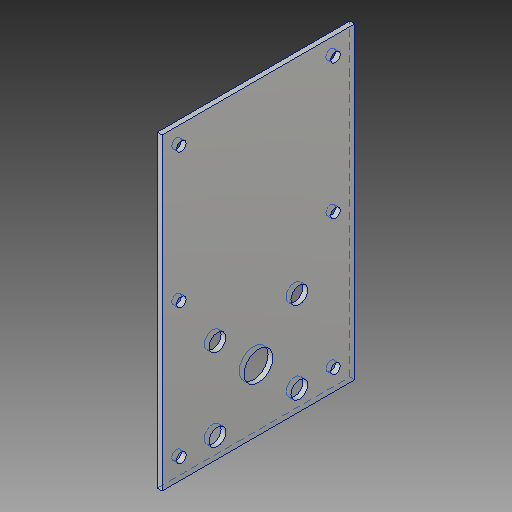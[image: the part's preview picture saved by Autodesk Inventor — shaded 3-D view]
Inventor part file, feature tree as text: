
AUTODESK INVENTOR PART (.ipt)
format: ipt  version: 2019 (Build 230136000, 136)  size: 129,536 bytes
history: native  units: in
note: dims shown in document units (in); Inventor stores cm internally (conversion verified against a paired STEP export)
features: extrude x3, sketch x3
ambient origin geometry x8: Origin, YZ Plane, XZ Plane, XY Plane, X Axis, Y Axis, Z Axis, Center Point
bodies: Solid1 (feature_tree)
feature tree (6):
  extrude  "Extrusion1"  Depth=5.0in
  extrude  "Extrusion2"  Depth=0.125in
  extrude  "Extrusion4"  Depth=0.125in
  sketch  "Sketch1"  dims[d0=8.0in d1=5.0in]
  sketch  "Sketch2"  dims[d2=0.125in d3=0.0in d4=3.0in]
  sketch  "Sketch4"  dims[d5=2.125in d6=0.4375in d8=0.75in d9=0.125in d10=0.0in d29=0.5in d30=1.0in d31=1.0in d32=0.25in d33=1.0in d34=0.0in]
